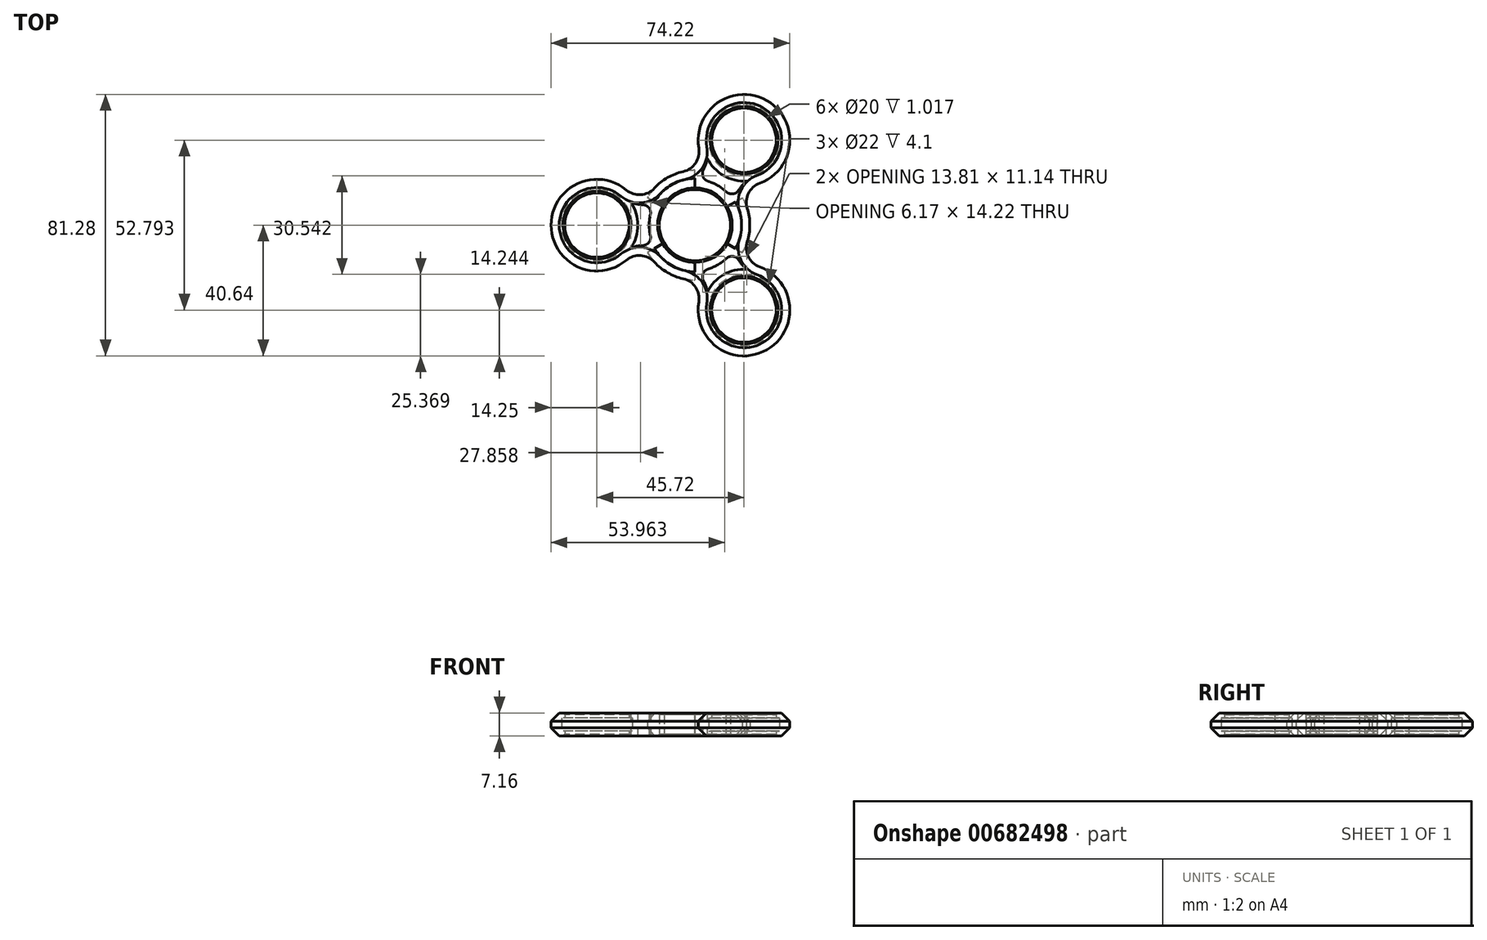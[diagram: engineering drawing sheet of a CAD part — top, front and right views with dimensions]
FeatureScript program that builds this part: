
annotation { "Feature Type Name" : "Feature", "Feature Type Description" : "" }
export const myFeature = defineFeature(function(context is Context, id is Id, definition is map)
    precondition{}
    {
        {
            var Q0;
            Q0=qCreatedBy(makeId("Top.planeOp"),FACE);
            var sketch = newSketch(context, id + "F0", { "sketchPlane" : qUnion([Q0])});
            skArc(sketch, "E0", {"start": v(0, 11.07) * mm, "mid": v(-11.07, 0) * mm, "end": v(0, -11.07) * mm});
            skArc(sketch, "E1", {"start": v(-12.58, -11.51) * mm, "mid": v(-6.87, -15.6) * mm, "end": v(0, -17.05) * mm});
            skCircle(sketch, "E2", {"center": v(-30.48, 0) * mm, "radius": 10 * mm});
            skArc(sketch, "E3", {"start": v(-21.34, 10.93) * mm, "mid": v(-44.73, 0) * mm, "end": v(-21.34, -10.93) * mm});
            skLineSegment(sketch, "E4", {"start": v(0, 17.05) * mm, "end": v(0, 11.07) * mm});
            skArc(sketch, "E5.trimOffspring", {"start": v(0, 17.05) * mm, "mid": v(-6.87, 15.6) * mm, "end": v(-12.58, 11.51) * mm});
            skLineSegment(sketch, "E6.trimOffspring", {"start": v(0, -11.07) * mm, "end": v(0, -17.05) * mm});
            skPoint(sketch, "E7.visualSharp", {"position": v(-16.68, 3.54) * mm});
            skArc(sketch, "E7.filletArc", {"start": v(-21.34, 10.93) * mm, "mid": v(-16.84, 9.46) * mm, "end": v(-12.58, 11.51) * mm});
            skPoint(sketch, "E8.visualSharp", {"position": v(-16.68, -3.54) * mm});
            skArc(sketch, "E8.filletArc", {"start": v(-12.58, -11.51) * mm, "mid": v(-16.84, -9.46) * mm, "end": v(-21.34, -10.93) * mm});
            skArc(sketch, "E9", {"start": v(-13.85, 3.23) * mm, "mid": v(-14.22, 0) * mm, "end": v(-13.85, -3.23) * mm});
            skArc(sketch, "E10", {"start": v(-19.96, -7.11) * mm, "mid": v(-17.96, -2.15) * mm, "end": v(-18.19, 3.2) * mm});
            skArc(sketch, "E11.trimOffspring", {"start": v(-16.3, -6.35) * mm, "mid": v(-18.17, -6.55) * mm, "end": v(-19.96, -7.11) * mm});
            skArc(sketch, "E12.filletArc", {"start": v(-16.05, 6.35) * mm, "mid": v(-16.08, 6.35) * mm, "end": v(-16.11, 6.34) * mm});
            skArc(sketch, "E13.filletArc", {"start": v(-16.3, -6.35) * mm, "mid": v(-14.33, -5.38) * mm, "end": v(-13.85, -3.23) * mm});
            skArc(sketch, "E14.MirrorCS", {"start": v(-16.3, 6.35) * mm, "mid": v(-18.17, 6.55) * mm, "end": v(-19.96, 7.11) * mm});
            skArc(sketch, "E15.MirrorCS", {"start": v(-19.96, 7.11) * mm, "mid": v(-17.96, 2.15) * mm, "end": v(-18.19, -3.2) * mm});
            skArc(sketch, "E16.MirrorCS", {"start": v(-16.3, 6.35) * mm, "mid": v(-14.33, 5.38) * mm, "end": v(-13.85, 3.23) * mm});
            skSolve(sketch);
        }
        {
            var Q0;
            Q0=makeQuery(id+"F0.imprint","IMPRINT",FACE,{"disambiguationData":[TD([[makeQuery(id+"F0.imprint","IMPRINT",EDGE,{"derivedFrom":sQuery(id+"F0.wireOp",EDGE,"E0")}),-1.0]])]});
            extrude(context, id + "F1", {"entities" : qUnion([Q0]), "endBound" : BoundingType.SYMMETRIC, "depth" : 7.15 * mm, "offsetDistance" : 25.4 * mm});
        }
        {
            var Q0;
            Q0=makeQuery(id+"F1.opExtrude","SWEPT_FACE",FACE,{"disambiguationData":[OSD([sQuery(id+"F0.wireOp",EDGE,"E3")])]});
            chamfer(context, id + "F2", {"entities" : qUnion([Q0]), "width" : 2.54 * mm, "tangentPropagation" : true});
        }
        {
            var Q0;
            Q0=makeQuery(id+"F1.opExtrude","CAP_EDGE",EDGE,{"disambiguationData":[OSD([sQuery(id+"F0.wireOp",EDGE,"E0")])],"isStart":false});
            var Q1;
            Q1=makeQuery(id+"F1.opExtrude","CAP_EDGE",EDGE,{"disambiguationData":[OSD([sQuery(id+"F0.wireOp",EDGE,"E0")])],"isStart":true});
            var Q2;
            Q2=makeQuery(id+"F1.opExtrude","CAP_EDGE",EDGE,{"disambiguationData":[OSD([sQuery(id+"F0.wireOp",EDGE,"E2")])],"isStart":false});
            var Q3;
            Q3=makeQuery(id+"F1.opExtrude","CAP_EDGE",EDGE,{"disambiguationData":[OSD([sQuery(id+"F0.wireOp",EDGE,"E2")])],"isStart":true});
            chamfer(context, id + "F3", {"entities" : qUnion([Q0, Q1, Q2, Q3]), "width" : 0.5 * mm, "tangentPropagation" : true});
        }
        {
            var Q0;
            Q0=qCreatedBy(makeId("Top.planeOp"),FACE);
            var sketch = newSketch(context, id + "F4", { "sketchPlane" : qUnion([Q0])});
            skCircle(sketch, "E17", {"center": v(-30.48, 0) * mm, "radius": 11 * mm});
            skSolve(sketch);
        }
        {
            var Q0;
            Q0=makeQuery(id+"F4.imprint","IMPRINT",FACE,{"disambiguationData":[TD([[makeQuery(id+"F4.imprint","IMPRINT",EDGE,{"derivedFrom":sQuery(id+"F4.wireOp",EDGE,"E17")}),1.0]])]});
            extrude(context, id + "F5", {"entities" : qUnion([Q0]), "operationType" : NewBodyOperationType.REMOVE, "endBound" : BoundingType.SYMMETRIC, "depth" : 4.1 * mm, "offsetDistance" : 25.4 * mm});
        }
        {
            var Q0;
            Q0=makeQuery(id+"F1.opExtrude","SWEPT_BODY",BODY,{"disambiguationData":[OSD([sQuery(id+"F0.wireOp",EDGE,"E0"),sQuery(id+"F0.wireOp",EDGE,"E1"),sQuery(id+"F0.wireOp",EDGE,"E2"),sQuery(id+"F0.wireOp",EDGE,"E3"),sQuery(id+"F0.wireOp",EDGE,"E4"),sQuery(id+"F0.wireOp",EDGE,"E5.trimOffspring"),sQuery(id+"F0.wireOp",EDGE,"E6.trimOffspring"),sQuery(id+"F0.wireOp",EDGE,"E7.filletArc"),sQuery(id+"F0.wireOp",EDGE,"E8.filletArc"),sQuery(id+"F0.wireOp",EDGE,"E9"),sQuery(id+"F0.wireOp",EDGE,"E10"),sQuery(id+"F0.wireOp",EDGE,"CQrigIKu-Oe8h-B1zI-lHb5-9fQeA1mbbMmQ"),sQuery(id+"F0.wireOp",EDGE,"E11.trimOffspring"),sQuery(id+"F0.wireOp",EDGE,"E12.filletArc"),sQuery(id+"F0.wireOp",EDGE,"E13.filletArc")])]});
            var Q1;
            Q1=makeQuery(id+"F1.opExtrude","SWEPT_FACE",FACE,{"disambiguationData":[OSD([sQuery(id+"F0.wireOp",EDGE,"E0")])]});
            circularPattern(context, id + "F6", {"entities" : qUnion([Q0]), "axis" : qUnion([Q1]), "angle" : 360 * degree, "instanceCount" : 3, "equalSpace" : true});
        }
    });
